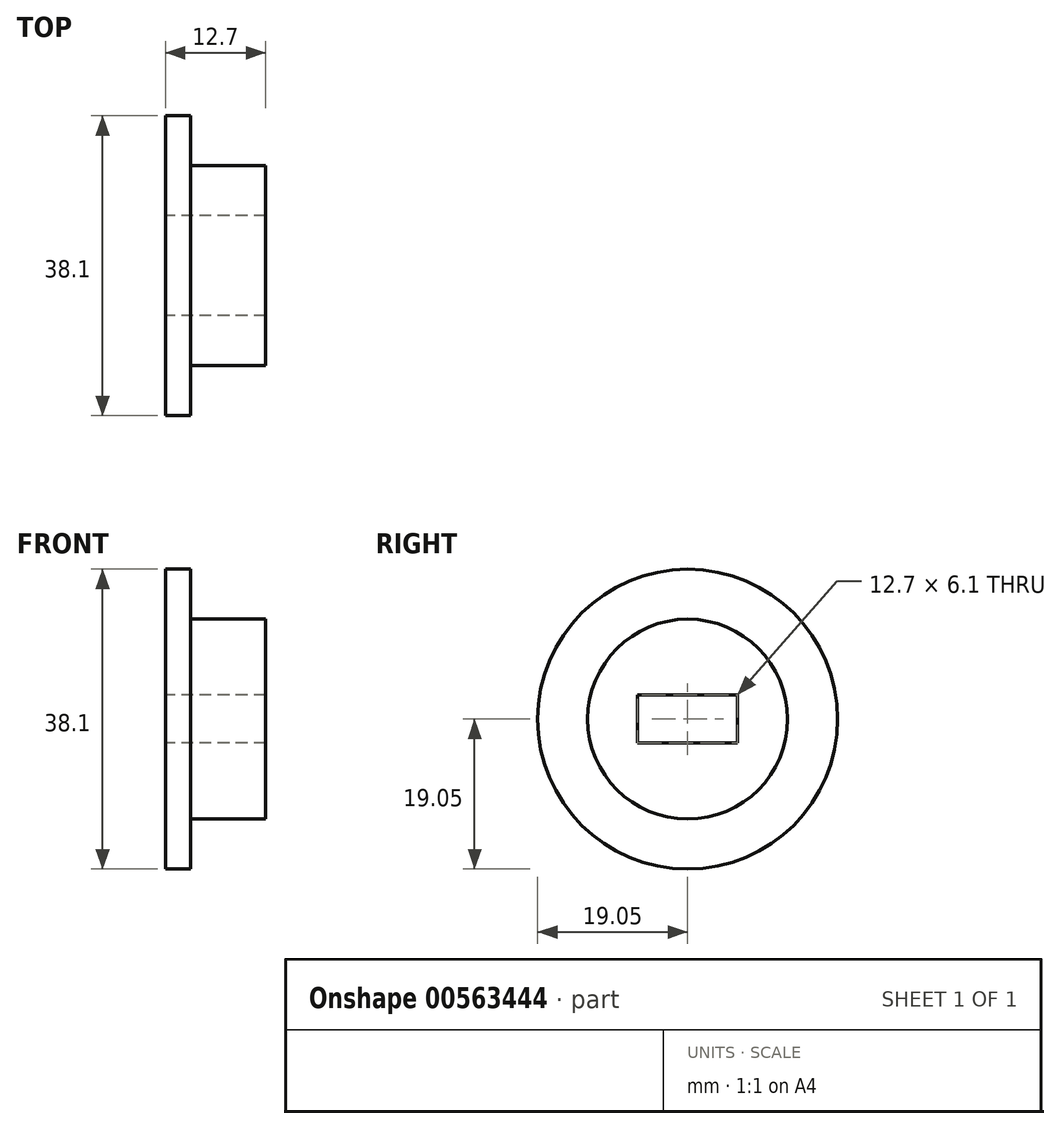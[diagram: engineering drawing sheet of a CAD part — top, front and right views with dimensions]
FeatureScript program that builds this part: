
annotation { "Feature Type Name" : "Feature", "Feature Type Description" : "" }
export const myFeature = defineFeature(function(context is Context, id is Id, definition is map)
    precondition{}
    {
        {
            var Q0;
            Q0=qCreatedBy(makeId("Right.planeOp"),FACE);
            var sketch = newSketch(context, id + "F0", { "sketchPlane" : qUnion([Q0])});
            skCircle(sketch, "E0", {"center": v(0, 0) * mm, "radius": 19.05 * mm});
            skSolve(sketch);
        }
        {
            var Q0;
            Q0=makeQuery(id+"F0.imprint","IMPRINT",FACE,{"disambiguationData":[TD([[makeQuery(id+"F0.imprint","IMPRINT",EDGE,{"derivedFrom":sQuery(id+"F0.wireOp",EDGE,"E0")}),1.0]])]});
            extrude(context, id + "F1", {"entities" : qUnion([Q0]), "depth" : 3.17 * mm, "offsetDistance" : 25.4 * mm});
        }
        {
            var Q0;
            Q0=makeQuery(id+"F1.opExtrude","CAP_FACE",FACE,{"disambiguationData":[OSD([sQuery(id+"F0.wireOp",EDGE,"E0")])],"isStart":false});
            var sketch = newSketch(context, id + "F2", { "sketchPlane" : qUnion([Q0])});
            skCircle(sketch, "E1", {"center": v(0, 0) * mm, "radius": 12.7 * mm});
            skSolve(sketch);
        }
        {
            var Q0;
            Q0 = qSketchRegion(id + "F2", true);
            extrude(context, id + "F3", {"entities" : qUnion([Q0]), "operationType" : NewBodyOperationType.ADD, "depth" : 9.52 * mm, "offsetDistance" : 25.4 * mm});
        }
        {
            var Q0;
            Q0=qCreatedBy(makeId("Right.planeOp"),FACE);
            var sketch = newSketch(context, id + "F4", { "sketchPlane" : qUnion([Q0])});
            skLineSegment(sketch, "E2.bottom", {"start": v(-6.35, 3.05) * mm, "end": v(6.35, 3.05) * mm});
            skLineSegment(sketch, "E2.top", {"start": v(-6.35, -3.05) * mm, "end": v(6.35, -3.05) * mm});
            skLineSegment(sketch, "E2.left", {"start": v(-6.35, 3.05) * mm, "end": v(-6.35, -3.05) * mm});
            skLineSegment(sketch, "E2.right", {"start": v(6.35, 3.05) * mm, "end": v(6.35, -3.05) * mm});
            skSolve(sketch);
        }
        {
            var Q0;
            Q0 = qSketchRegion(id + "F4", true);
            var Q1;
            Q1 = qConstructionFilter(qBodyType(qCreatedBy(id + "F4" ,EDGE), BodyType.WIRE), ConstructionObject.NO);
            extrude(context, id + "F5", {"entities" : qUnion([Q0]), "operationType" : NewBodyOperationType.REMOVE, "surfaceEntities" : qUnion([Q1]), "endBound" : BoundingType.THROUGH_ALL, "depth" : 25.4 * mm, "offsetDistance" : 25.4 * mm});
        }
    });
